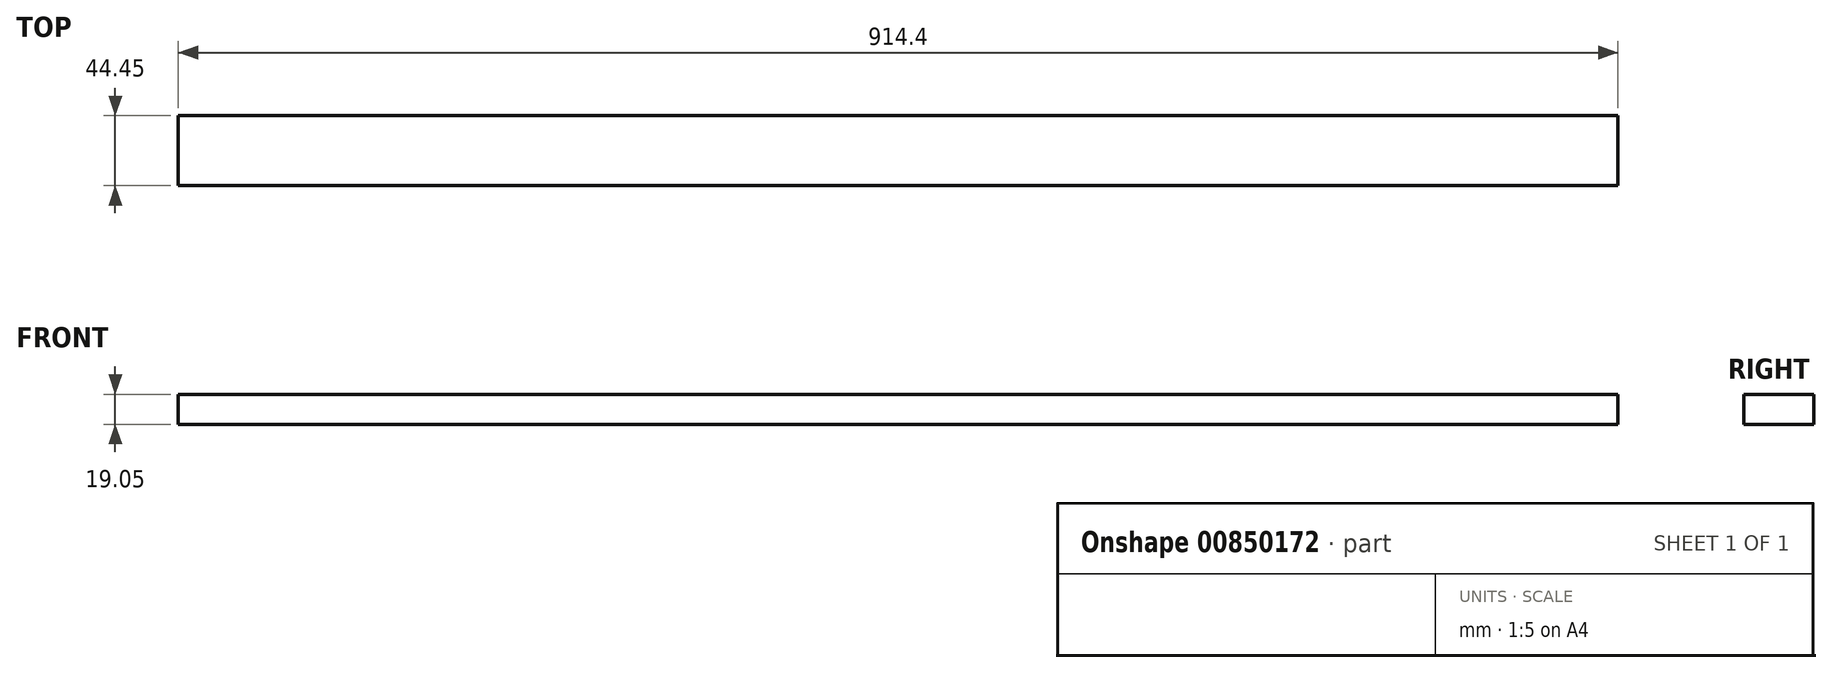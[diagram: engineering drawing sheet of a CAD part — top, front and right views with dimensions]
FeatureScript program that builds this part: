
annotation { "Feature Type Name" : "Feature", "Feature Type Description" : "" }
export const myFeature = defineFeature(function(context is Context, id is Id, definition is map)
    precondition{}
    {
        {
            var Q0;
            Q0=qCreatedBy(makeId("Front.planeOp"),FACE);
            var sketch = newSketch(context, id + "F0", { "sketchPlane" : qUnion([Q0])});
            skLineSegment(sketch, "E0.bottom", {"start": v(457.2, -26.8) * mm, "end": v(-457.2, -26.8) * mm});
            skLineSegment(sketch, "E0.top", {"start": v(457.2, -7.76) * mm, "end": v(-457.2, -7.76) * mm});
            skLineSegment(sketch, "E0.left", {"start": v(457.2, -26.8) * mm, "end": v(457.2, -7.76) * mm});
            skLineSegment(sketch, "E0.right", {"start": v(-457.2, -26.8) * mm, "end": v(-457.2, -7.76) * mm});
            skPoint(sketch, "E0.middle", {"position": v(0, -17.28) * mm});
            skSolve(sketch);
        }
        {
            var Q0;
            Q0 = qSketchRegion(id + "F0", true);
            extrude(context, id + "F1", {"entities" : qUnion([Q0]), "depth" : 44.45 * mm, "offsetDistance" : 25.4 * mm});
        }
    });
